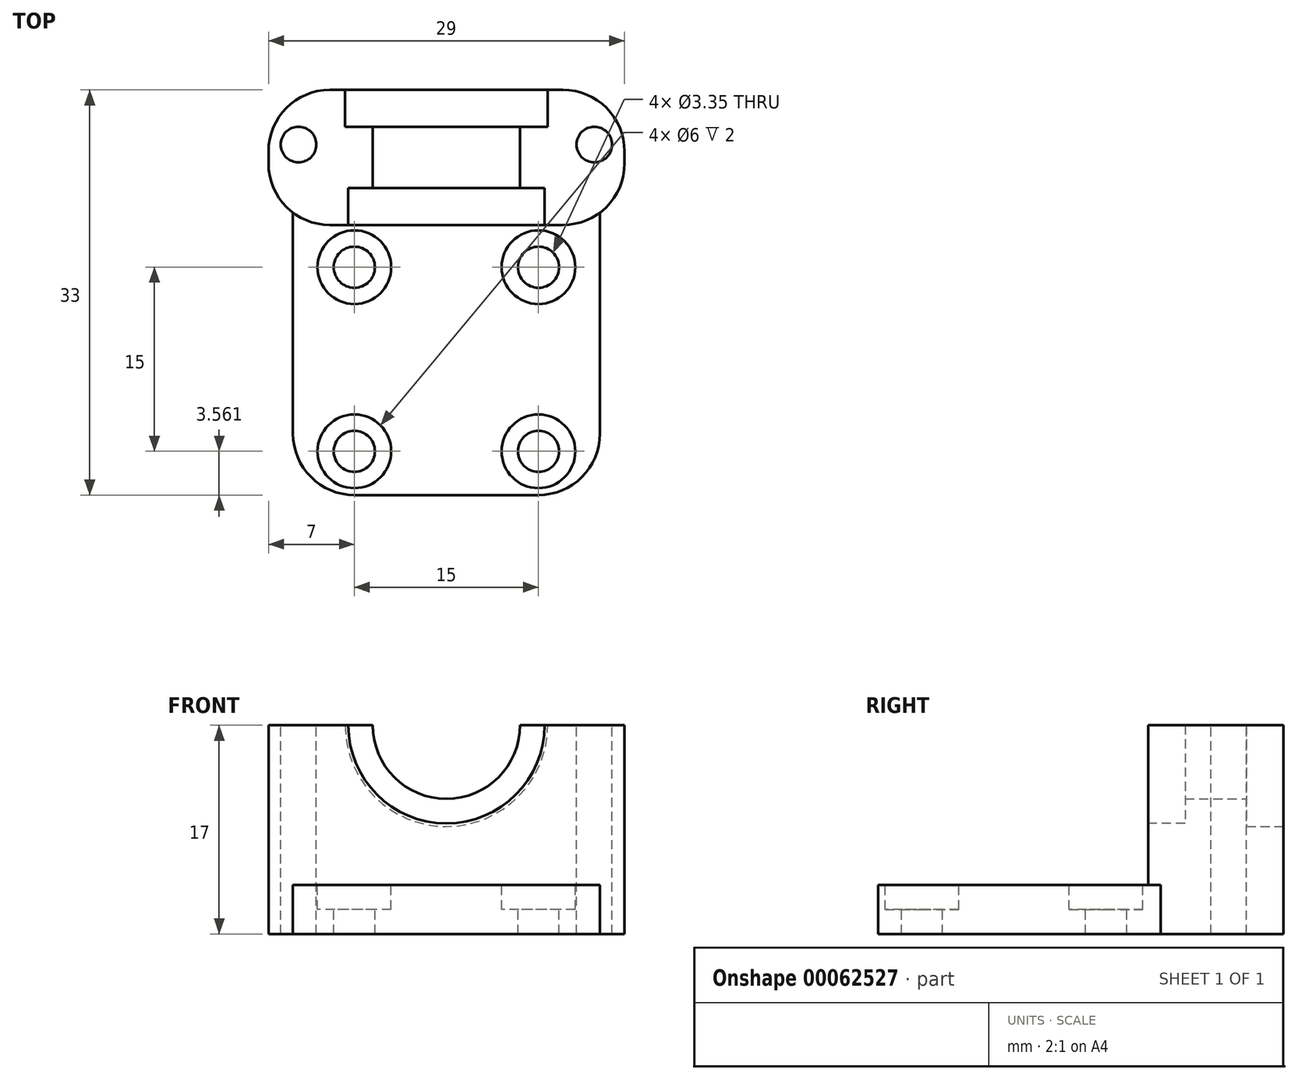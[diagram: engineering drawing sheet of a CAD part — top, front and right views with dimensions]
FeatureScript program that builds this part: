
annotation { "Feature Type Name" : "Feature", "Feature Type Description" : "" }
export const myFeature = defineFeature(function(context is Context, id is Id, definition is map)
    precondition{}
    {
        {
            var Q0;
            Q0=qCreatedBy(makeId("Top.planeOp"),FACE);
            var sketch = newSketch(context, id + "F0", { "sketchPlane" : qUnion([Q0])});
            skLineSegment(sketch, "E0.bottom", {"start": v(0, 0) * mm, "end": v(25, 0) * mm});
            skLineSegment(sketch, "E0.top", {"start": v(0, 33) * mm, "end": v(25, 33) * mm});
            skLineSegment(sketch, "E0.left", {"start": v(0, 0) * mm, "end": v(0, 33) * mm});
            skLineSegment(sketch, "E0.right", {"start": v(25, 0) * mm, "end": v(25, 33) * mm});
            skSolve(sketch);
        }
        {
            var Q0;
            Q0=qSketchRegion(id+"F0",true);
            extrude(context, id + "F1", {"entities" : qUnion([Q0]), "depth" : 4 * mm});
        }
        {
            var Q0;
            Q0=makeQuery(id+"F1.opExtrude","CAP_FACE",FACE,{"disambiguationData":[OSD([sQuery(id+"F0.wireOp",EDGE,"E0.bottom"),sQuery(id+"F0.wireOp",EDGE,"E0.top"),sQuery(id+"F0.wireOp",EDGE,"E0.left"),sQuery(id+"F0.wireOp",EDGE,"E0.right")])],"isStart":false});
            var sketch = newSketch(context, id + "F2", { "sketchPlane" : qUnion([Q0])});
            skCircle(sketch, "E1", {"center": v(5, 18.56) * mm, "radius": 1.68 * mm});
            skCircle(sketch, "E2", {"center": v(20, 18.56) * mm, "radius": 1.68 * mm});
            skCircle(sketch, "E3", {"center": v(5, 3.56) * mm, "radius": 1.68 * mm});
            skCircle(sketch, "E4", {"center": v(20, 3.56) * mm, "radius": 1.68 * mm});
            skLineSegment(sketch, "E5", {"start": v(5, 18.56) * mm, "end": v(0, 18.56) * mm});
            skLineSegment(sketch, "E6", {"start": v(20, 3.56) * mm, "end": v(25, 3.56) * mm});
            skCircle(sketch, "E7", {"center": v(5, 18.56) * mm, "radius": 3 * mm});
            skCircle(sketch, "E8", {"center": v(20, 18.56) * mm, "radius": 3 * mm});
            skCircle(sketch, "E9", {"center": v(5, 3.56) * mm, "radius": 3 * mm});
            skCircle(sketch, "E10", {"center": v(20, 3.56) * mm, "radius": 3 * mm});
            skSolve(sketch);
        }
        {
            var Q0;
            Q0=makeQuery(id+"F2.imprint","IMPRINT",FACE,{"disambiguationData":[TD([[makeQuery(id+"F2.imprint","IMPRINT",EDGE,{"derivedFrom":sQuery(id+"F2.wireOp",EDGE,"E1")}),1.0]])]});
            var Q1;
            Q1=makeQuery(id+"F2.imprint","IMPRINT",FACE,{"disambiguationData":[TD([[makeQuery(id+"F2.imprint","IMPRINT",EDGE,{"derivedFrom":sQuery(id+"F2.wireOp",EDGE,"E2")}),1.0]])]});
            var Q2;
            Q2=makeQuery(id+"F2.imprint","IMPRINT",FACE,{"disambiguationData":[TD([[makeQuery(id+"F2.imprint","IMPRINT",EDGE,{"derivedFrom":sQuery(id+"F2.wireOp",EDGE,"E4")}),1.0]])]});
            var Q3;
            Q3=makeQuery(id+"F2.imprint","IMPRINT",FACE,{"disambiguationData":[TD([[makeQuery(id+"F2.imprint","IMPRINT",EDGE,{"derivedFrom":sQuery(id+"F2.wireOp",EDGE,"E3")}),1.0]])]});
            extrude(context, id + "F3", {"entities" : qUnion([Q0, Q1, Q2, Q3]), "operationType" : NewBodyOperationType.REMOVE, "oppositeDirection" : true, "depth" : 25 * mm});
        }
        {
            var Q0;
            Q0=makeQuery(id+"F1.opExtrude","CAP_FACE",FACE,{"disambiguationData":[OSD([sQuery(id+"F0.wireOp",EDGE,"E0.bottom"),sQuery(id+"F0.wireOp",EDGE,"E0.top"),sQuery(id+"F0.wireOp",EDGE,"E0.left"),sQuery(id+"F0.wireOp",EDGE,"E0.right")])],"isStart":false});
            var sketch = newSketch(context, id + "F4", { "sketchPlane" : qUnion([Q0])});
            skLineSegment(sketch, "E11.bottom", {"start": v(0, 33) * mm, "end": v(25, 33) * mm});
            skLineSegment(sketch, "E11.top", {"start": v(0, 22) * mm, "end": v(25, 22) * mm});
            skLineSegment(sketch, "E11.left", {"start": v(0, 33) * mm, "end": v(0, 22) * mm});
            skLineSegment(sketch, "E11.right", {"start": v(25, 33) * mm, "end": v(25, 22) * mm});
            skSolve(sketch);
        }
        {
            var Q0;
            Q0=qSketchRegion(id+"F4",true);
            extrude(context, id + "F5", {"entities" : qUnion([Q0]), "operationType" : NewBodyOperationType.ADD, "depth" : 13 * mm});
        }
        {
            var Q0;
            Q0=makeQuery(id+"F5.boolean.opBoolean","MERGE",FACE,{"derivedFrom":[makeQuery(id+"F1.opExtrude","SWEPT_FACE",FACE,{"disambiguationData":[OSD([sQuery(id+"F0.wireOp",EDGE,"E0.top")])]}),makeQuery(id+"F5.opExtrude","SWEPT_FACE",FACE,{"disambiguationData":[OSD([sQuery(id+"F4.wireOp",EDGE,"E11.bottom")])]})]});
            var sketch = newSketch(context, id + "F6", { "sketchPlane" : qUnion([Q0])});
            skCircle(sketch, "E12", {"center": v(-12.5, 17) * mm, "radius": 6 * mm});
            skSolve(sketch);
        }
        {
            var Q0;
            {var subQ0=makeQuery(id+"F5.opExtrude","CAP_EDGE",EDGE,{"disambiguationData":[OSD([sQuery(id+"F4.wireOp",EDGE,"E11.bottom")])],"isStart":false});var subQ1=sQuery(id+"F6.wireOp",EDGE,"E12");var subQ3=makeQuery(id+"F6.imprint","INTERSECT",VERTEX,{"disambiguationData":[OD(0.0)],"derivedFrom":[subQ0,subQ1]});Q0=makeQuery(id+"F6.imprint","IMPRINT",FACE,{"disambiguationData":[TD([[makeQuery(id+"F6.imprint","IMPRINT",EDGE,{"disambiguationData":[TD([[subQ3,1.0]])],"derivedFrom":subQ1}),1.0]])]});}
            extrude(context, id + "F7", {"entities" : qUnion([Q0]), "operationType" : NewBodyOperationType.REMOVE, "oppositeDirection" : true, "depth" : 9 * mm});
        }
        {
            var Q0;
            Q0=makeQuery(id+"F5.opExtrude","SWEPT_FACE",FACE,{"disambiguationData":[OSD([sQuery(id+"F4.wireOp",EDGE,"E11.top")])]});
            var sketch = newSketch(context, id + "F8", { "sketchPlane" : qUnion([Q0])});
            skCircle(sketch, "E13", {"center": v(12.5, 17) * mm, "radius": 8 * mm});
            skSolve(sketch);
        }
        {
            var Q0;
            Q0=qSketchRegion(id+"F8",true);
            extrude(context, id + "F9", {"entities" : qUnion([Q0]), "operationType" : NewBodyOperationType.REMOVE, "oppositeDirection" : true, "depth" : 3 * mm});
        }
        {
            var Q0;
            Q0=makeQuery(id+"F2.imprint","IMPRINT",FACE,{"disambiguationData":[TD([[makeQuery(id+"F2.imprint","IMPRINT",EDGE,{"derivedFrom":sQuery(id+"F2.wireOp",EDGE,"E1")}),-1.0]])]});
            var Q1;
            Q1=makeQuery(id+"F2.imprint","IMPRINT",FACE,{"disambiguationData":[TD([[makeQuery(id+"F2.imprint","IMPRINT",EDGE,{"derivedFrom":sQuery(id+"F2.wireOp",EDGE,"E2")}),-1.0]])]});
            var Q2;
            Q2=makeQuery(id+"F2.imprint","IMPRINT",FACE,{"disambiguationData":[TD([[makeQuery(id+"F2.imprint","IMPRINT",EDGE,{"derivedFrom":sQuery(id+"F2.wireOp",EDGE,"E4")}),-1.0]])]});
            var Q3;
            Q3=makeQuery(id+"F2.imprint","IMPRINT",FACE,{"disambiguationData":[TD([[makeQuery(id+"F2.imprint","IMPRINT",EDGE,{"derivedFrom":sQuery(id+"F2.wireOp",EDGE,"E3")}),-1.0]])]});
            extrude(context, id + "F10", {"entities" : qUnion([Q0, Q1, Q2, Q3]), "operationType" : NewBodyOperationType.REMOVE, "oppositeDirection" : true, "depth" : 2 * mm});
        }
        {
            var Q0;
            Q0=makeQuery(id+"F1.opExtrude","SWEPT_EDGE",EDGE,{"disambiguationData":[OSD([sQuery(id+"F0.wireOp",EDGE,"E0.bottom"),sQuery(id+"F0.wireOp",EDGE,"E0.left")])]});
            var Q1;
            Q1=makeQuery(id+"F1.opExtrude","SWEPT_EDGE",EDGE,{"disambiguationData":[OSD([sQuery(id+"F0.wireOp",EDGE,"E0.bottom"),sQuery(id+"F0.wireOp",EDGE,"E0.right")])]});
            fillet(context, id + "F11", {"entities" : qUnion([Q0, Q1]), "radius" : 5 * mm, "tangentPropagation" : true, "allowEdgeOverflow" : false});
        }
        {
            var Q0;
            Q0=makeQuery(id+"F5.boolean.opBoolean","MERGE",FACE,{"derivedFrom":[makeQuery(id+"F1.opExtrude","SWEPT_FACE",FACE,{"disambiguationData":[OSD([sQuery(id+"F0.wireOp",EDGE,"E0.left")])]}),makeQuery(id+"F5.opExtrude","SWEPT_FACE",FACE,{"disambiguationData":[OSD([sQuery(id+"F4.wireOp",EDGE,"E11.left")])]})]});
            var sketch = newSketch(context, id + "F12", { "sketchPlane" : qUnion([Q0])});
            skLineSegment(sketch, "E14.bottom", {"start": v(-33, 0) * mm, "end": v(-22, 0) * mm});
            skLineSegment(sketch, "E14.top", {"start": v(-33, 17) * mm, "end": v(-22, 17) * mm});
            skLineSegment(sketch, "E14.left", {"start": v(-33, 0) * mm, "end": v(-33, 17) * mm});
            skLineSegment(sketch, "E14.right", {"start": v(-22, 0) * mm, "end": v(-22, 17) * mm});
            skSolve(sketch);
        }
        {
            var Q0;
            Q0=qSketchRegion(id+"F12",true);
            extrude(context, id + "F13", {"entities" : qUnion([Q0]), "operationType" : NewBodyOperationType.ADD, "depth" : 2 * mm});
        }
        {
            var Q0;
            Q0=makeQuery(id+"F5.boolean.opBoolean","MERGE",FACE,{"derivedFrom":[makeQuery(id+"F1.opExtrude","SWEPT_FACE",FACE,{"disambiguationData":[OSD([sQuery(id+"F0.wireOp",EDGE,"E0.right")])]}),makeQuery(id+"F5.opExtrude","SWEPT_FACE",FACE,{"disambiguationData":[OSD([sQuery(id+"F4.wireOp",EDGE,"E11.right")])]})]});
            var sketch = newSketch(context, id + "F14", { "sketchPlane" : qUnion([Q0])});
            skLineSegment(sketch, "E15.bottom", {"start": v(33, 0) * mm, "end": v(22, 0) * mm});
            skLineSegment(sketch, "E15.top", {"start": v(33, 17) * mm, "end": v(22, 17) * mm});
            skLineSegment(sketch, "E15.left", {"start": v(33, 0) * mm, "end": v(33, 17) * mm});
            skLineSegment(sketch, "E15.right", {"start": v(22, 0) * mm, "end": v(22, 17) * mm});
            skSolve(sketch);
        }
        {
            var Q0;
            Q0=qSketchRegion(id+"F14",true);
            extrude(context, id + "F15", {"entities" : qUnion([Q0]), "operationType" : NewBodyOperationType.ADD, "depth" : 2 * mm});
        }
        {
            var Q0;
            {var subQ0=sQuery(id+"F4.wireOp",EDGE,"E11.bottom");var subQ1=sQuery(id+"F4.wireOp",EDGE,"E11.top");var subQ2=sQuery(id+"F4.wireOp",EDGE,"E11.left");Q0=makeQuery(id+"F9.boolean.opBoolean","SPLIT",FACE,{"disambiguationData":[TD([makeQuery(id+"F1.opExtrude","SWEPT_FACE",FACE,{"disambiguationData":[OSD([sQuery(id+"F0.wireOp",EDGE,"E0.left")])]})])],"derivedFrom":makeQuery(id+"F5.opExtrude","CAP_FACE",FACE,{"disambiguationData":[OSD([subQ0,subQ1,subQ2,sQuery(id+"F4.wireOp",EDGE,"E11.right")])],"isStart":false})});}
            var sketch = newSketch(context, id + "F16", { "sketchPlane" : qUnion([Q0])});
            skCircle(sketch, "E16", {"center": v(0.45, 28.55) * mm, "radius": 1.45 * mm});
            skCircle(sketch, "E17", {"center": v(24.55, 28.55) * mm, "radius": 1.45 * mm});
            skSolve(sketch);
        }
        {
            var Q0;
            Q0=qSketchRegion(id+"F16",true);
            extrude(context, id + "F17", {"entities" : qUnion([Q0]), "operationType" : NewBodyOperationType.REMOVE, "oppositeDirection" : true, "depth" : 25 * mm});
        }
        {
            var Q0;
            Q0=makeQuery(id+"F13.opExtrude","CAP_EDGE",EDGE,{"disambiguationData":[OSD([sQuery(id+"F12.wireOp",EDGE,"E14.right")])],"isStart":false});
            var Q1;
            Q1=makeQuery(id+"F13.opExtrude","CAP_EDGE",EDGE,{"disambiguationData":[OSD([sQuery(id+"F12.wireOp",EDGE,"E14.left")])],"isStart":false});
            var Q2;
            Q2=makeQuery(id+"F15.opExtrude","CAP_EDGE",EDGE,{"disambiguationData":[OSD([sQuery(id+"F14.wireOp",EDGE,"E15.left")])],"isStart":false});
            var Q3;
            Q3=makeQuery(id+"F15.opExtrude","CAP_EDGE",EDGE,{"disambiguationData":[OSD([sQuery(id+"F14.wireOp",EDGE,"E15.right")])],"isStart":false});
            fillet(context, id + "F18", {"entities" : qUnion([Q0, Q1, Q2, Q3]), "radius" : 5 * mm, "tangentPropagation" : true, "allowEdgeOverflow" : false});
        }
        {
            var Q0;
            Q0=makeQuery(id+"F15.boolean.opBoolean","MERGE",FACE,{"derivedFrom":[makeQuery(id+"F13.boolean.opBoolean","MERGE",FACE,{"derivedFrom":[makeQuery(id+"F5.boolean.opBoolean","MERGE",FACE,{"derivedFrom":[makeQuery(id+"F1.opExtrude","SWEPT_FACE",FACE,{"disambiguationData":[OSD([sQuery(id+"F0.wireOp",EDGE,"E0.top")])]}),makeQuery(id+"F5.opExtrude","SWEPT_FACE",FACE,{"disambiguationData":[OSD([sQuery(id+"F4.wireOp",EDGE,"E11.bottom")])]})]}),makeQuery(id+"F13.opExtrude","SWEPT_FACE",FACE,{"disambiguationData":[OSD([sQuery(id+"F12.wireOp",EDGE,"E14.left")])]})]}),makeQuery(id+"F15.opExtrude","SWEPT_FACE",FACE,{"disambiguationData":[OSD([sQuery(id+"F14.wireOp",EDGE,"E15.left")])]})]});
            var sketch = newSketch(context, id + "F19", { "sketchPlane" : qUnion([Q0])});
            skCircle(sketch, "E18", {"center": v(-12.5, 17) * mm, "radius": 8.25 * mm});
            skSolve(sketch);
        }
        {
            var Q0;
            Q0 = qSketchRegion(id + "F19", true);
            extrude(context, id + "F20", {"entities" : qUnion([Q0]), "operationType" : NewBodyOperationType.REMOVE, "oppositeDirection" : true, "depth" : 3 * mm});
        }
    });
